# Revit family: БА220_RV17_LOD400 (04.11.23)
name_source: partatom
category: Электрооборудование
revit_build: Autodesk Revit 2017 (Build: 20170118_1100(x64)
units: mm (PartAtom-declared; Revit-internal decimal feet)

## family parameters
Всегда вертикально = Нет
Конфигурация панели = Два столбца, слева направо
На основе рабочей плоскости = Да
Общий = Нет
При загрузке вырезать с полостями = Нет
Размер круглого соединителя = Использовать диаметр
Тип детали = Щит
Точка расчета площади = Нет

## types (1)
- БА220
    ADSK_URL страницы изделия = https://stilsoft.ru
    ADSK_Единица измерения = шт.
    ADSK_Завод-изготовитель = ООО «Основа Безопасности»
    ADSK_Количество = 1
    ADSK_Марка = СТВФ.426471.016
    ADSK_Масса = 1.2
    ADSK_Наименование = Трансляционный аудиоусилитель БА220
    ADSK_Размер_Высота = 55 мм
    ADSK_Размер_Глубина = 155 мм
    ADSK_Размер_Длина = 262 мм
    d_короба = 20 мм
    Время непрерывной работы, ч = круглосуточно
    Диапазон воспроизводимых частот, Гц = 20... 20000
    Долговременная выходная мощность, Вт = 2 х 25
    Количество аудиоканалов, шт = 2
    Коэффициент усиления по напряжению Au, дБ = 34
    Мощность = 50
    Напряжение = 220
    Отметка по умолчанию = 1219 мм
    Потребляемый ток, не более, А = 1 А
